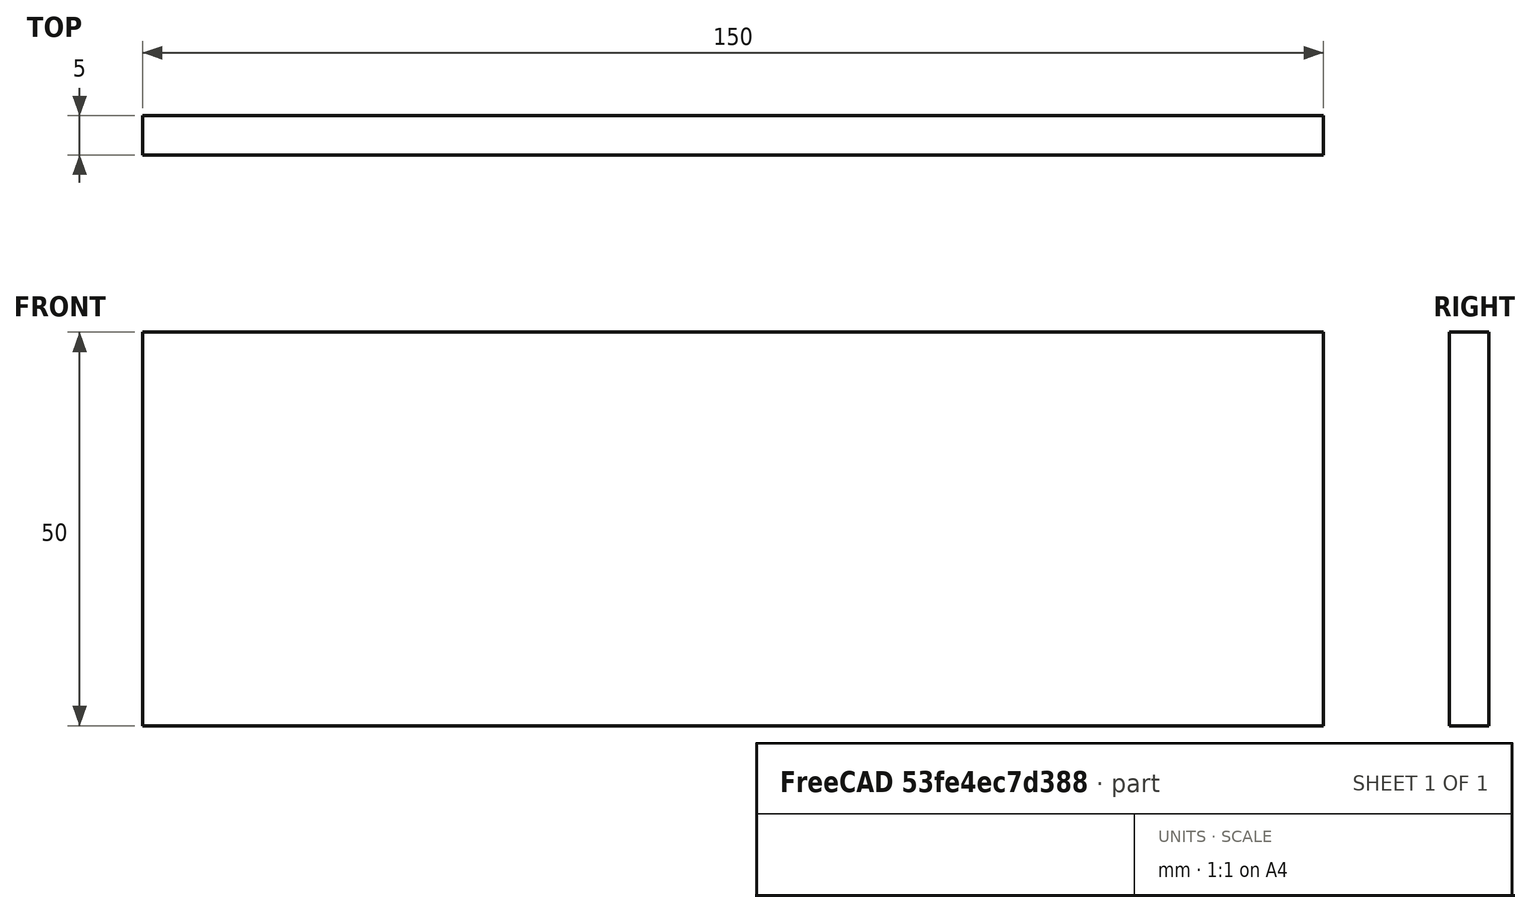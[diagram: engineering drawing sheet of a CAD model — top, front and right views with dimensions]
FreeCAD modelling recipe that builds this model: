
FCSTD DOCUMENT  (FreeCAD 0.15R4671 (Git))
Label: Flat Bar 150x5 EN10058 S235JR
License: All rights reserved
LicenseURL: http://en.wikipedia.org/wiki/All_rights_reserved
objects: Sketcher::SketchObject×1, Part::Extrusion×1
note: 2 computed .brp shape members not serialized (recipe doc carries the construction recipe); baked Part::Feature solids carry a one-line shape summary decoded from their .brp

FEATURE [Sketcher::SketchObject] Sketch
  sketch-geometry (4):
    g0: LineSegment StartX=-75 StartY=-2.5 StartZ=0 EndX=75 EndY=-2.5 EndZ=0
    g1: LineSegment StartX=75 StartY=-2.5 StartZ=0 EndX=75 EndY=2.5 EndZ=0
    g2: LineSegment StartX=75 StartY=2.5 StartZ=0 EndX=-75 EndY=2.5 EndZ=0
    g3: LineSegment StartX=-75 StartY=2.5 StartZ=0 EndX=-75 EndY=-2.5 EndZ=0
  constraints (12):
    c: Coincident(g0,g1)
    c: Coincident(g1,g2)
    c: Coincident(g2,g3)
    c: Coincident(g3,g0)
    c: Horizontal(g0)
    c: Horizontal(g2)
    c: Vertical(g1)
    c: Vertical(g3)
    c: Symmetric(g1,g2,g-2)
    c: Symmetric(g0,g1,g-1)
    c: DistanceY(g1) = 5
    c: DistanceX(g0) = 150
FEATURE [Part::Extrusion] Extrude  label="Flat Bar 150x5 EN10058 S235JR"
  Base = -> Sketch
  Dir = (0,0,50)
  Solid = true
